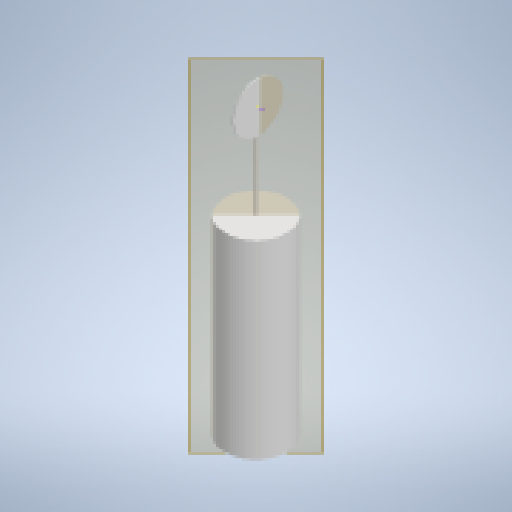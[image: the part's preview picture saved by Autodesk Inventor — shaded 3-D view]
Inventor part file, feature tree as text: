
AUTODESK INVENTOR PART (.ipt)
format: ipt  version: 2024.2 (Build 282272000, 272)  size: 148,480 bytes
history: native  units: in
note: dims shown in document units (in); Inventor stores cm internally (conversion verified against a paired STEP export)
features: extrude x3, plane x3, sketch x1
ambient origin geometry x8: Origin, YZ Plane, XZ Plane, XY Plane, X Axis, Y Axis, Z Axis, Center Point
bodies: Solid1 (feature_tree)
feature tree (7):
  extrude  "Extrusion1"  Depth=1.925in TaperAngle=0.0deg
  extrude  "Extrusion2"  Depth=0.011in
  sketch  "Sketch3"  dims[d0=0.625in d1=1.925in d2=0.0in d3=0.022in d4=0.96in d5=0.0in d6=0.502in d7=0.011in d8=0.0in]
  plane  "Work Plane1"
  extrude  "Extrusion3"  Depth=0.96in TaperAngle=0.0deg
  plane  "Work Plane4"
  plane  "Work Plane3"
